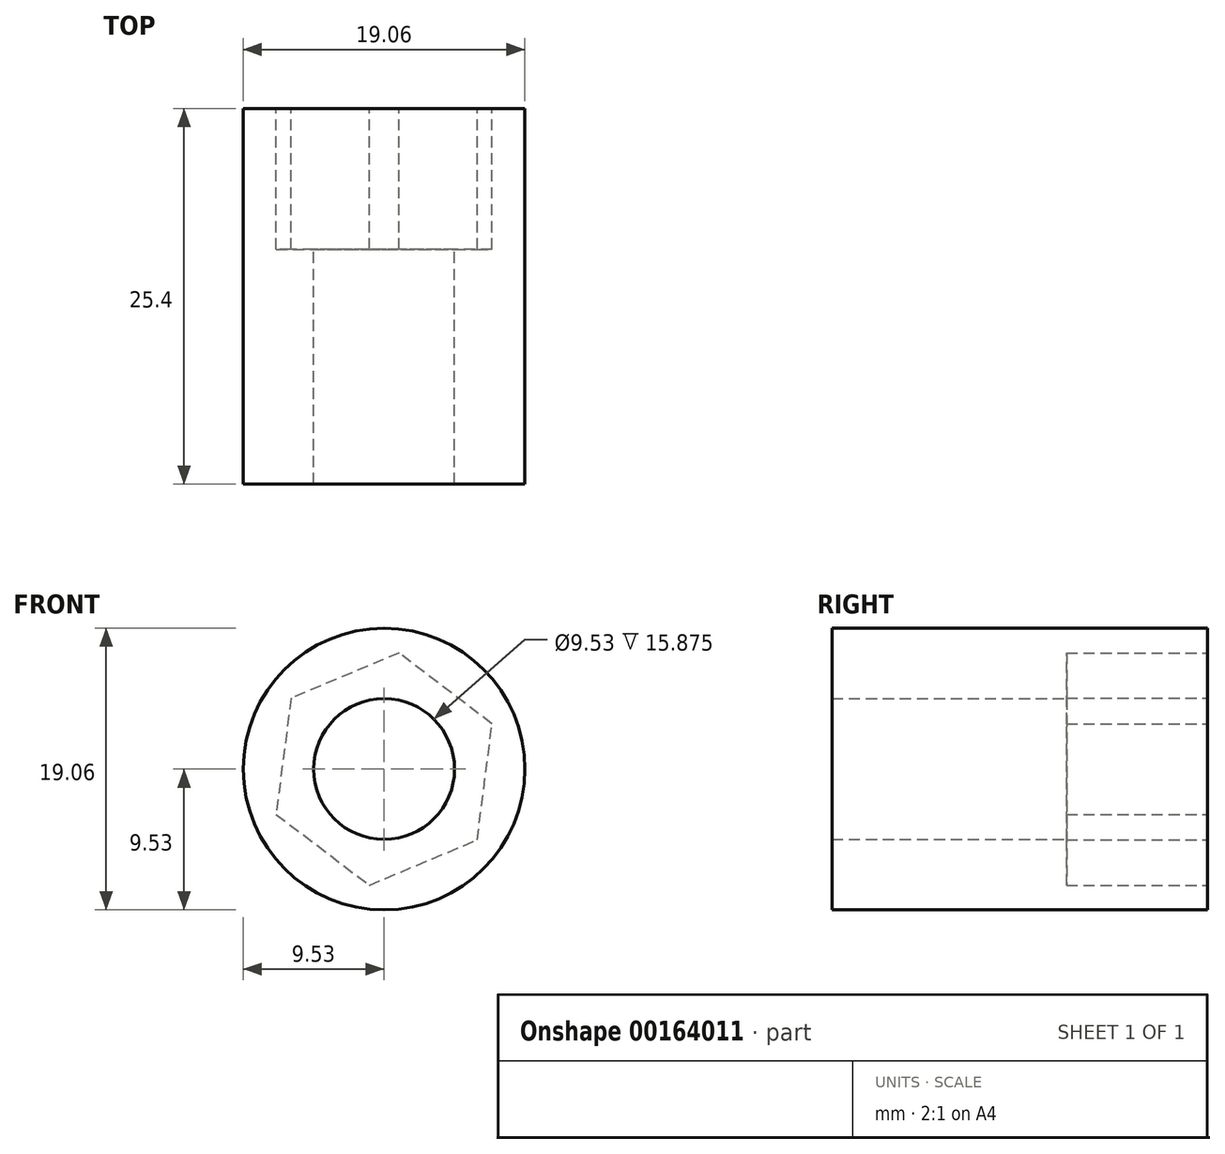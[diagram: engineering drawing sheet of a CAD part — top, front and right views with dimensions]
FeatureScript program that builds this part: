
annotation { "Feature Type Name" : "Feature", "Feature Type Description" : "" }
export const myFeature = defineFeature(function(context is Context, id is Id, definition is map)
    precondition{}
    {
        {
            var Q0;
            Q0=qCreatedBy(makeId("Front.planeOp"),FACE);
            var sketch = newSketch(context, id + "F0", { "sketchPlane" : qUnion([Q0])});
            skCircle(sketch, "E0", {"center": v(0, 0) * mm, "radius": 9.53 * mm});
            skSolve(sketch);
        }
        {
            var Q0;
            Q0=makeQuery(id+"F0.imprint","IMPRINT",FACE,{"disambiguationData":[TD([[makeQuery(id+"F0.imprint","IMPRINT",EDGE,{"derivedFrom":sQuery(id+"F0.wireOp",EDGE,"E0")}),1.0]])]});
            extrude(context, id + "F1", {"entities" : qUnion([Q0]), "depth" : 25.4 * mm});
        }
        {
            var Q0;
            Q0=qCreatedBy(makeId("Front.planeOp"),FACE);
            var sketch = newSketch(context, id + "F2", { "sketchPlane" : qUnion([Q0])});
            skLineSegment(sketch, "E1.bottom", {"start": v(4.76, -4.76) * mm, "end": v(-4.76, -4.76) * mm});
            skLineSegment(sketch, "E1.top", {"start": v(4.76, 4.76) * mm, "end": v(-4.76, 4.76) * mm});
            skLineSegment(sketch, "E1.left", {"start": v(4.76, -4.76) * mm, "end": v(4.76, 4.76) * mm});
            skLineSegment(sketch, "E1.right", {"start": v(-4.76, -4.76) * mm, "end": v(-4.76, 4.76) * mm});
            skPoint(sketch, "E1.middle", {"position": v(0, 0) * mm});
            skCircle(sketch, "E2", {"center": v(0, 0) * mm, "radius": 4.76 * mm});
            skSolve(sketch);
        }
        {
            var Q0;
            {var subQ0=sQuery(id+"F2.wireOp",EDGE,"E2");var subQ1=makeQuery(id+"F2.imprint","INTERSECT",VERTEX,{"derivedFrom":[sQuery(id+"F2.wireOp",EDGE,"E1.top"),subQ0]});Q0=makeQuery(id+"F2.imprint","IMPRINT",FACE,{"disambiguationData":[TD([[makeQuery(id+"F2.imprint","IMPRINT",EDGE,{"disambiguationData":[TD([[subQ1,1.0]])],"derivedFrom":subQ0}),1.0]])]});}
            extrude(context, id + "F3", {"entities" : qUnion([Q0]), "operationType" : NewBodyOperationType.REMOVE, "endBound" : BoundingType.THROUGH_ALL, "depth" : 25.4 * mm});
        }
        {
            var Q0;
            Q0 = qSketchRegion(id + "F2", true);
            extrude(context, id + "F4", {"entities" : qUnion([Q0]), "operationType" : NewBodyOperationType.REMOVE, "oppositeDirection" : true, "depth" : 11.1 * mm});
        }
        {
            var Q0;
            Q0=makeQuery(id+"F1.opExtrude","CAP_FACE",FACE,{"disambiguationData":[OSD([sQuery(id+"F0.wireOp",EDGE,"E0")])],"isStart":true});
            var sketch = newSketch(context, id + "F5", { "sketchPlane" : qUnion([Q0])});
            skCircle(sketch, "E3.cCircle", {"center": v(0, 0) * mm, "radius": 6.86 * mm, "construction": true});
            skLineSegment(sketch, "E3.0", {"start": v(7.3, -3.06) * mm, "end": v(1, -7.85) * mm});
            skLineSegment(sketch, "E3.1", {"start": v(1, -7.85) * mm, "end": v(-6.3, -4.8) * mm});
            skLineSegment(sketch, "E3.2", {"start": v(-6.3, -4.8) * mm, "end": v(-7.3, 3.06) * mm});
            skLineSegment(sketch, "E3.3", {"start": v(-7.3, 3.06) * mm, "end": v(-1, 7.85) * mm});
            skLineSegment(sketch, "E3.4", {"start": v(-1, 7.85) * mm, "end": v(6.3, 4.8) * mm});
            skLineSegment(sketch, "E3.5", {"start": v(6.3, 4.8) * mm, "end": v(7.3, -3.06) * mm});
            skPoint(sketch, "E3.0.midPoint", {"position": v(4.15, -5.46) * mm});
            skSolve(sketch);
        }
        {
            var Q0;
            Q0 = qSketchRegion(id + "F5", true);
            extrude(context, id + "F6", {"entities" : qUnion([Q0]), "operationType" : NewBodyOperationType.REMOVE, "oppositeDirection" : true, "depth" : 9.52 * mm});
        }
    });
